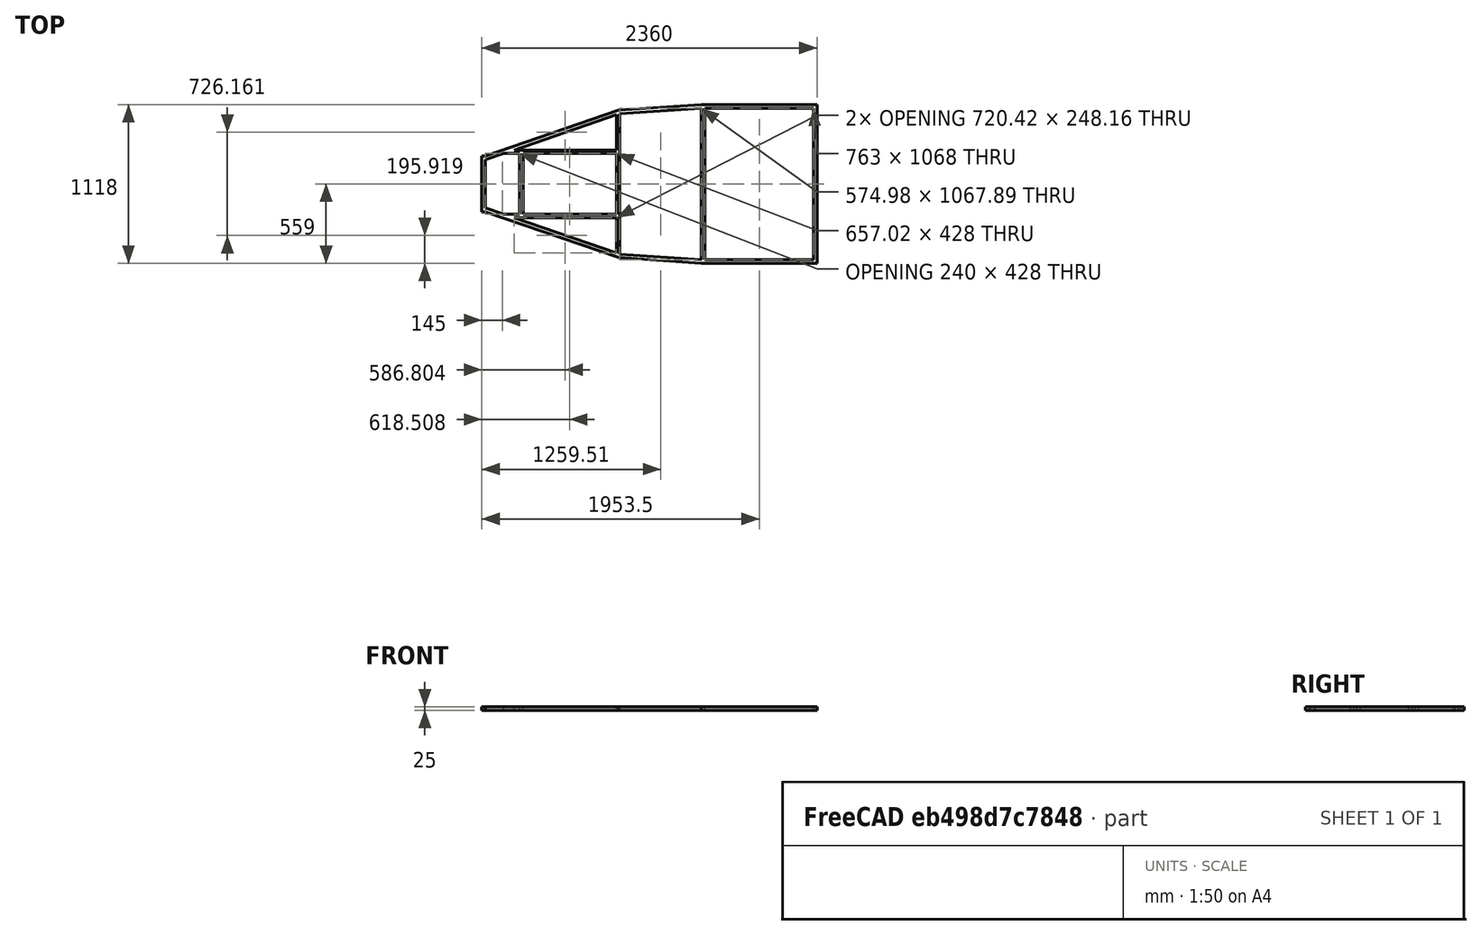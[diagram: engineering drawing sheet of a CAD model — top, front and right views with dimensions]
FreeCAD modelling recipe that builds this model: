
FCSTD DOCUMENT  (FreeCAD 0.21R33771 (Git))
Label: Base
License: All rights reserved
LicenseURL: http://en.wikipedia.org/wiki/All_rights_reserved
objects: Sketcher::SketchObject×1, PartDesign::Pad×1, PartDesign::Body×1
note: 4 computed .brp shape members not serialized (recipe doc carries the construction recipe); baked Part::Feature solids carry a one-line shape summary decoded from their .brp

FEATURE [Sketcher::SketchObject] Sketch
  FullyConstrained = true
  MapMode = 5
  Support = -> [XY_Plane]
  sketch-geometry (37):
    g0: LineSegment StartX=0 StartY=0 StartZ=0 EndX=-813 EndY=0 EndZ=0
    g1: LineSegment StartX=-813 StartY=0 StartZ=0 EndX=-813 EndY=1118 EndZ=0
    g2: LineSegment StartX=-813 StartY=1118 StartZ=0 EndX=0 EndY=1118 EndZ=0
    g3: LineSegment StartX=0 StartY=1118 StartZ=0 EndX=0 EndY=0 EndZ=0
    g4: LineSegment StartX=-813 StartY=1118 StartZ=0 EndX=-1395.67 EndY=1078.57 EndZ=0
    g5: LineSegment StartX=-1395.67 StartY=1078.57 StartZ=0 EndX=-2335 EndY=755 EndZ=0
    g6: LineSegment StartX=-813 StartY=0 StartZ=0 EndX=-1395.67 EndY=39.4321 EndZ=0
    g7: LineSegment StartX=-1395.67 StartY=39.4321 StartZ=0 EndX=-2335 EndY=363 EndZ=0
    g8: LineSegment StartX=-2335 StartY=755 StartZ=0 EndX=-2360 EndY=755 EndZ=0
    g9: LineSegment StartX=-2335 StartY=363 StartZ=0 EndX=-2360 EndY=363 EndZ=0
    g10: LineSegment StartX=-2360 StartY=755 StartZ=0 EndX=-2360 EndY=363 EndZ=0
    g11: LineSegment StartX=-2360 StartY=755 StartZ=0 EndX=0 EndY=0 EndZ=0
    g12: LineSegment StartX=0 StartY=1118 StartZ=0 EndX=-2360 EndY=363 EndZ=0
    g13: LineSegment StartX=-2335 StartY=728.558 StartZ=0 EndX=-2335 EndY=389.442 EndZ=0
    g14: LineSegment StartX=-2335 StartY=728.558 StartZ=0 EndX=-2205.98 EndY=773 EndZ=0
    g15: LineSegment StartX=-2335 StartY=389.442 StartZ=0 EndX=-2205.98 EndY=345 EndZ=0
    g16: LineSegment StartX=-2205.98 StartY=345 StartZ=0 EndX=-2095 EndY=345 EndZ=0
    g17: LineSegment StartX=-2205.98 StartY=773 StartZ=0 EndX=-2095 EndY=773 EndZ=0
    g18: LineSegment StartX=-2095 StartY=773 StartZ=0 EndX=-2095 EndY=345 EndZ=0
    g19: LineSegment StartX=-2070 StartY=773 StartZ=0 EndX=-2070 EndY=345 EndZ=0
    g20: LineSegment StartX=-2070 StartY=773 StartZ=0 EndX=-1412.98 EndY=773 EndZ=0
    g21: LineSegment StartX=-2133.41 StartY=798 StartZ=0 EndX=-1412.98 EndY=1046.16 EndZ=0
    g22: LineSegment StartX=-2133.41 StartY=798 StartZ=0 EndX=-1412.98 EndY=798 EndZ=0
    g23: LineSegment StartX=-2133.41 StartY=320 StartZ=0 EndX=-1412.98 EndY=320 EndZ=0
    g24: LineSegment StartX=-2133.41 StartY=320 StartZ=0 EndX=-1412.98 EndY=71.8387 EndZ=0
    g25: LineSegment StartX=-1412.98 StartY=1046.16 StartZ=0 EndX=-1412.98 EndY=798 EndZ=0
    g26: LineSegment StartX=-1387.98 StartY=1054.03 StartZ=0 EndX=-1387.98 EndY=63.9693 EndZ=0
    g27: LineSegment StartX=-1412.98 StartY=773 StartZ=0 EndX=-1412.98 EndY=345 EndZ=0
    g28: LineSegment StartX=-1412.98 StartY=345 StartZ=0 EndX=-2070 EndY=345 EndZ=0
    g29: LineSegment StartX=-1412.98 StartY=71.8387 StartZ=0 EndX=-1412.98 EndY=320 EndZ=0
    g30: LineSegment StartX=-1387.98 StartY=1054.03 StartZ=0 EndX=-813 EndY=1092.94 EndZ=0
    g31: LineSegment StartX=-813 StartY=1092.94 StartZ=0 EndX=-813 EndY=25.0572 EndZ=0
    g32: LineSegment StartX=-813 StartY=25.0572 StartZ=0 EndX=-1387.98 EndY=63.9693 EndZ=0
    g33: LineSegment StartX=-788 StartY=1093 StartZ=0 EndX=-788 EndY=25 EndZ=0
    g34: LineSegment StartX=-788 StartY=25 StartZ=0 EndX=-25 EndY=25 EndZ=0
    g35: LineSegment StartX=-25 StartY=25 StartZ=0 EndX=-25 EndY=1093 EndZ=0
    g36: LineSegment StartX=-25 StartY=1093 StartZ=0 EndX=-788 EndY=1093 EndZ=0
  constraints (107):
    c: Coincident(g0,g1)
    c: Coincident(g1,g2)
    c: Coincident(g2,g3)
    c: Coincident(g3,g0)
    c: Horizontal(g0)
    c: Horizontal(g2)
    c: Vertical(g1)
    c: Vertical(g3)
    c: Coincident(g0,g-1)
    c: DistanceY(g3,g3) = 1118
    c: Coincident(g4,g1)
    c: Coincident(g5,g4)
    c: Coincident(g6,g0)
    c: Coincident(g7,g6)
    c: Equal(g6,g4)
    c: Equal(g5,g7)
    c: Coincident(g8,g5)
    c: Horizontal(g8)
    c: Coincident(g9,g7)
    c: Horizontal(g9)
    c: Coincident(g10,g8)
    c: Coincident(g10,g9)
    c: Vertical(g10)
    c: Equal(g9,g8)
    c: Coincident(g11,g8)
    c: Coincident(g11,g0)
    c: Coincident(g12,g2)
    c: Coincident(g12,g9)
    c: Equal(g11,g12)
    c: DistanceX(g8,g8) = 25
    c: DistanceX(g9,g2) = 2360
    c: Vertical(g13)
    c: Coincident(g14,g13)
    c: Coincident(g15,g13)
    c: Coincident(g16,g15)
    c: Horizontal(g16)
    c: Coincident(g17,g14)
    c: Horizontal(g17)
    c: Coincident(g18,g17)
    c: Coincident(g18,g16)
    c: Vertical(g18)
    c: Vertical(g19)
    c: Coincident(g20,g19)
    c: Horizontal(g20)
    c: Coincident(g22,g21)
    c: Horizontal(g22)
    c: Horizontal(g23)
    c: Coincident(g24,g23)
    c: Coincident(g25,g21)
    c: Coincident(g25,g22)
    c: Vertical(g25)
    c: Vertical(g26)
    c: Coincident(g27,g20)
    c: Vertical(g27)
    c: Coincident(g28,g27)
    c: Coincident(g28,g19)
    c: Horizontal(g28)
    c: Coincident(g29,g24)
    c: Coincident(g29,g23)
    c: Vertical(g29)
    c: Coincident(g30,g26)
    c: Coincident(g31,g30)
    c: Vertical(g31)
    c: Coincident(g32,g31)
    c: Coincident(g32,g26)
    c: Vertical(g33)
    c: Coincident(g34,g33)
    c: Horizontal(g34)
    c: Coincident(g35,g34)
    c: Vertical(g35)
    c: Coincident(g36,g35)
    c: Coincident(g36,g33)
    c: Horizontal(g36)
    c: DistanceX(g35,g2) = 25
    c: DistanceY(g35,g2) = 25
    c: DistanceY(g0,g34) = 25
    c: Parallel(g14,g5)
    c: Distance(g5,g14) = 25
    c: Distance(g7,g15) = 25
    c: DistanceX(g8,g13) = 25
    c: DistanceX(g17,g19) = 25
    c: DistanceY(g19,g21) = 25
    c: DistanceY(g17,g21) = 25
    c: DistanceY(g23,g16) = 25
    c: DistanceY(g23,g19) = 25
    c: DistanceX(g21,g26) = 25
    c: DistanceX(g20,g26) = 25
    c: DistanceX(g24,g26) = 25
    c: Parallel(g32,g6)
    c: Parallel(g30,g4)
    c: Distance(g30,g4) = 25
    c: Distance(g21,g5) = 25
    c: Parallel(g21,g5)
    c: Parallel(g24,g7)
    c: Distance(g23,g7) = 25
    c: Parallel(g15,g7)
    c: Distance(g31,g6) = 25
    c: Distance(g30,g33) = 25
    c: PointOnObject(g2,g31)
    c: DistanceY(g10,g10) = 392
    c: Equal(g17,g16)
    c: Distance(g4) = 584
    c: Distance(g5) = 993.5
    c: DistanceX(g14,g20) = 793
    c: DistanceY(g19,g19) = 428
    c: DistanceX(g16,g0) = 2095
    c: DistanceX(g0,g0) = 813
FEATURE [PartDesign::Pad] Pad
  Direction = (0,0,1)
  Length = 25
  Length2 = 10
  Profile = -> Sketch
  ReferenceAxis = -> Sketch [N_Axis]
  Type = 0
FEATURE [PartDesign::Body] Body
  Group = -> [Sketch,Pad]
  Origin = -> Origin
  Tip = -> Pad
